# Revit family: AGS-Remote-Panic-Buttons
name_source: partatom
category: Generic Models
units: mm (PartAtom-declared; Revit-internal decimal feet)

## family parameters
Always vertical = Yes
Can host rebar = No
Cut with Voids When Loaded = No
Maintain Annotation Orientation = No
Part Type = Normal
Room Calculation Point = No
Round Connector Dimension = Use Diameter
Shared = No
Work Plane-Based = No

## types (18) — shared parameters
APPROVALS & WARRANTY = Three year guarantee against breakage of polycarbonate in normal use 
(one year on electro mechanical and electronic components).
BLUE = BLUE
Construction = Station housing molded of tough 
polycarbonate.
·  UL Listed to U.S. and Canadian 
safety standards.
Default Elevation = 0.00 in
Description = The AGS-EGOTW, multipurpose push button to be used 
for a wide range of applications with the AGS Merlin range 
of gas safety systems
Design = Unique, curved design helps 
protect against accidental 
activation.
General Information = Multipurpose push button switches 
cover a wide range of applications 
both indoors and outdoors.
Installation = 5VA flammability rating on backplate 
and spacer.
·  Typical working properties of 
polycarbonate are -40° to 250°F 
(-40° to 121°C).
Manufacturer = American Gas Safety LLC
Options = Your choice of colors — red, green, 
yellow, white or blue.
RED = RED
URL = https://americangassafety.com
YELLOW = YELLOW

## per-type parameters (varying)
| type | BLUE BODY | Emergency Boiler Shut Off | Emergency Gas Shut Off | Emergency Power Off | KEY TYPE | PUSH BUTTON | RED BODY | YELLOW BODY |
| AGS EGO TW Y A | No | No | Yes | No | No | Yes | No | Yes |
| AGS EGO TW R A | No | No | Yes | No | No | Yes | Yes | No |
| AGS EGO TW B A | Yes | No | Yes | No | No | Yes | No | No |
| AGS EGO KL Y A | No | No | Yes | No | Yes | No | No | Yes |
| AGS EGO KL R A | No | No | Yes | No | Yes | No | Yes | No |
| AGS EGO KL B A | Yes | No | Yes | No | Yes | No | No | No |
| AGS EPO TW Y A | No | No | No | Yes | No | Yes | No | Yes |
| AGS EPO TW R A | No | No | No | Yes | No | Yes | Yes | No |
| AGS EPO TW B A | Yes | No | No | Yes | No | Yes | No | No |
| AGS EPO KL Y A | No | No | No | Yes | Yes | No | No | Yes |
| AGS EPO KL R A | No | No | No | Yes | Yes | No | Yes | No |
| AGS EPO KL B A | Yes | No | No | Yes | Yes | No | No | No |
| AGS EBO TW Y A | No | Yes | No | No | No | Yes | No | Yes |
| AGS EBO TW R A | No | Yes | No | No | No | Yes | Yes | No |
| AGS EBO TW B A | Yes | Yes | No | No | No | Yes | No | No |
| AGS EBO KL Y A | No | Yes | No | No | Yes | No | No | Yes |
| AGS EBO KL R A | No | Yes | No | No | Yes | No | Yes | No |
| AGS EBO KL B A | Yes | Yes | No | No | Yes | No | No | No |

## geometry (parser evidence)
native form markers: Sweep x2
no freeform markers — native parametric forms only
